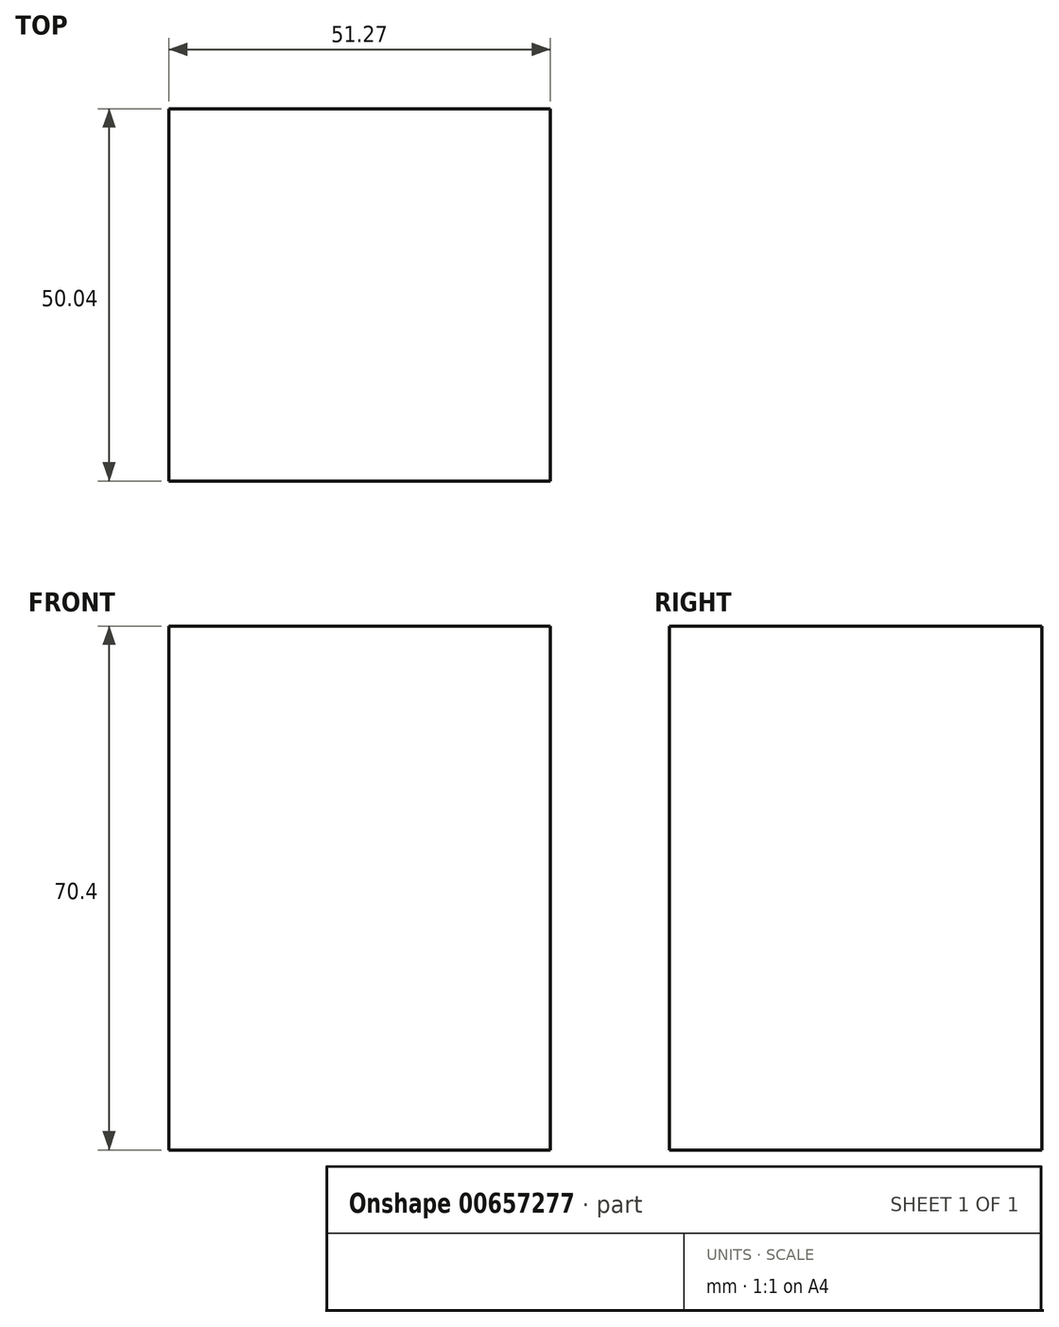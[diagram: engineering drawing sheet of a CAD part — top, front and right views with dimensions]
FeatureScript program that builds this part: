
annotation { "Feature Type Name" : "Feature", "Feature Type Description" : "" }
export const myFeature = defineFeature(function(context is Context, id is Id, definition is map)
    precondition{}
    {
        {
            var Q0;
            Q0=qCreatedBy(makeId("Top.planeOp"),FACE);
            var sketch = newSketch(context, id + "F0", { "sketchPlane" : qUnion([Q0])});
            skLineSegment(sketch, "E0.bottom", {"start": v(-31.62, 24.7) * mm, "end": v(19.65, 24.7) * mm});
            skLineSegment(sketch, "E0.top", {"start": v(-31.62, -25.35) * mm, "end": v(19.65, -25.35) * mm});
            skLineSegment(sketch, "E0.left", {"start": v(-31.62, 24.7) * mm, "end": v(-31.62, -25.35) * mm});
            skLineSegment(sketch, "E0.right", {"start": v(19.65, 24.7) * mm, "end": v(19.65, -25.35) * mm});
            skSolve(sketch);
        }
        {
            var Q0;
            Q0=makeQuery(id+"F0.imprint","IMPRINT",FACE,{"disambiguationData":[TD([[makeQuery(id+"F0.imprint","IMPRINT",EDGE,{"derivedFrom":sQuery(id+"F0.wireOp",EDGE,"E0.bottom")}),-1.0]])]});
            extrude(context, id + "F1", {"entities" : qUnion([Q0]), "depth" : 70.4 * mm, "offsetDistance" : 25 * mm});
        }
    });
